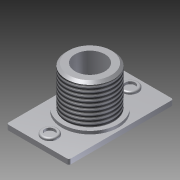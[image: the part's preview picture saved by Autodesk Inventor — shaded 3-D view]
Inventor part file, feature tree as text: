
AUTODESK INVENTOR PART (.ipt)
format: ipt  version: 2011 SP1 (Build 150282100, 282)  size: 160,256 bytes
history: native  units: in
note: dims shown in document units (in); Inventor stores cm internally (conversion verified against a paired STEP export)
features: other x35, sketch x5, revolve x3, extrude x2, thread x1
ambient origin geometry x8: Origin, YZ Plane, XZ Plane, XY Plane, X Axis, Y Axis, Z Axis, Center Point
bodies: Solid1 (feature_tree)
feature tree (46):
  extrude  "Extrusion1"  TaperAngle=360.0deg  [1 undecoded]
  revolve  "Revolution1"  [1 undecoded]
  thread  "Thread1"  [1 undecoded]
  extrude  "Extrusion2"  [1 undecoded]
  revolve  "Revolution2"  [1 undecoded]
  revolve  "Revolution3"  [1 undecoded]
  other  "hex_face_nut_XY"
  other  "hex_face_nut_YZ"
  other  "hex_face_nut_ZX"
  other  "hex_face_nut_X"
  other  "hex_face_nut_Y"
  other  "hex_face_nut_Z"
  other  "hex_face_nut_Center"
  other  "knurled_nut_XY"
  other  "knurled_nut_YZ"
  other  "knurled_nut_ZX"
  other  "knurled_nut_X"
  other  "knurled_nut_Y"
  other  "knurled_nut_Z"
  other  "knurled_nut_Center"
  other  "lockwasher_XY"
  other  "lockwasher_YZ"
  other  "lockwasher_ZX"
  other  "lockwasher_X"
  other  "lockwasher_Y"
  other  "lockwasher_Z"
  other  "lockwasher_Center"
  other  "panel_XY"
  other  "panel_YZ"
  other  "panel_ZX"
  other  "panel_X"
  other  "panel_Y"
  other  "panel_Z"
  other  "panel_Center"
  other  "toggle_XY"
  other  "toggle_YZ"
  other  "toggle_ZX"
  other  "toggle_X"
  other  "toggle_Y"
  other  "toggle_Z"
  other  "toggle_Center"
  sketch  "Sketch_1"  dims[d0=0.05in d1=0.0in d2=360.0deg]
  sketch  "Sketch_4"
  sketch  "Sketch_6"
  sketch  "Sketch_2"  dims[d3=0.3648in d4=0.0in d5=1.0in d6=0.0in d7=360.0deg]
  sketch  "Sketch_3"  dims[d8=360.0deg]
note: 6 required parameter values undecoded (feature->parameter linkage not recoverable at this tier; creation-order binding heuristic only, values carry confidence <= 0.55)